# Revit family: Thorn CARAT
name_source: partatom
category: Lighting Fixtures
revit_build: Autodesk Revit 2018 (Build: 20170223_1515(x64)
units: mm (PartAtom-declared; Revit-internal decimal feet)

## family parameters
Always vertical = Yes
Cut with Voids When Loaded = No
Light Source = Yes
OmniClass Number = 23.80.70.14
OmniClass Title = Luminaries for External Lighting
Part Type = Normal
Room Calculation Point = No
Round Connector Dimension = Use Diameter
Shared = No
Work Plane-Based = Yes

## types (2) — shared parameters
Color Filter = 16777215
Description = LED urban luminaire
Dimming Lamp Color Temperature Shift = <None>
Emit Shape Visible in Rendering = No
Lamp = LED
Manufacturer = Thorn Lighting
Tilt Angle = 90.00°
Voltage = 230 V
zero-valued in all types: Default Elevation

## per-type parameters (varying)
| type | Apparent Load | CT L NR | CT S NR | Emit from Circle Diameter | Height | Length | Ligt Source Offset | Model | Photometric Web File | URL | Width |
| CT S NR | 11 VA | No | Yes | 415 mm | 81 mm  [stored 0.265748 ft] | 435 mm  [stored 1.42717 ft] | 218 mm | 96635141 | 96635141_(STD).ies | www.thornlighting.com/96635141 | 435 mm  [stored 1.42717 ft] |
| CT L NR | 50 VA | Yes | No | 490 mm | 87 mm  [stored 0.285433 ft] | 510 mm  [stored 1.67323 ft] | 255 mm  [stored 0.836614 ft] | 96635162 | 96635162_(STD).IES | www.thornlighting.com/96635162 | 510 mm  [stored 1.67323 ft] |

note: [stored X ft] marks values corroborated as IEEE doubles in the binary element streams (Revit-internal decimal feet)

## geometry (parser evidence)
native form markers: Sweep x7
no freeform markers — native parametric forms only
